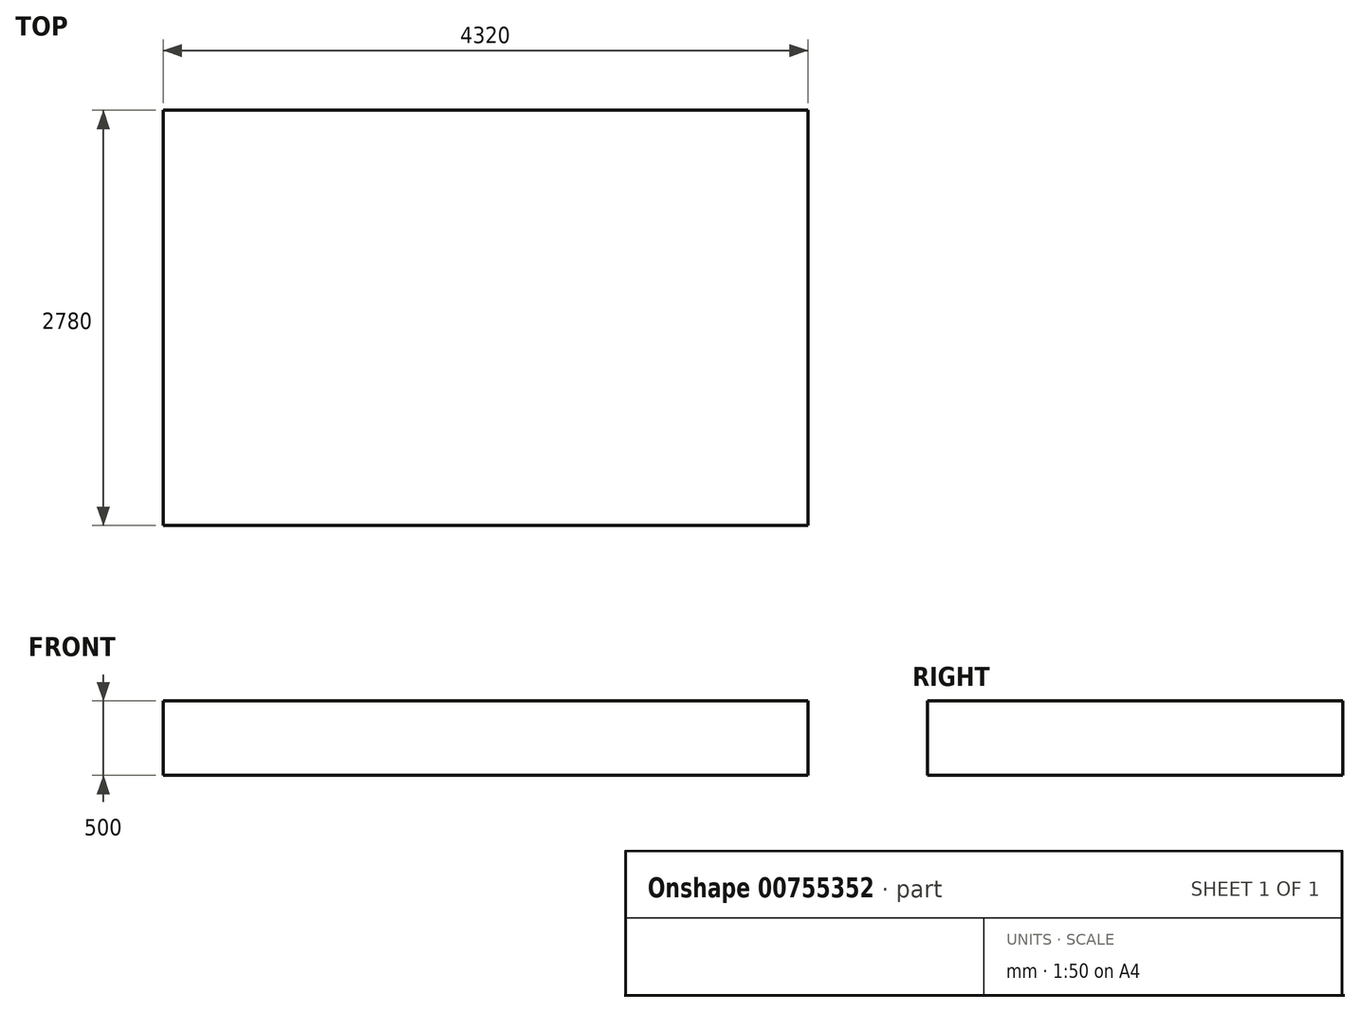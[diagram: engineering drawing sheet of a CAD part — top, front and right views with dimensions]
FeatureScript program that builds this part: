
annotation { "Feature Type Name" : "Feature", "Feature Type Description" : "" }
export const myFeature = defineFeature(function(context is Context, id is Id, definition is map)
    precondition{}
    {
        {
            var Q0;
            Q0=qCreatedBy(makeId("Top.planeOp"),FACE);
            var sketch = newSketch(context, id + "F0", { "sketchPlane" : qUnion([Q0])});
            skLineSegment(sketch, "E0.bottom", {"start": v(-2160, 1390) * mm, "end": v(2160, 1390) * mm});
            skLineSegment(sketch, "E0.top", {"start": v(-2160, -1390) * mm, "end": v(2160, -1390) * mm});
            skLineSegment(sketch, "E0.left", {"start": v(-2160, 1390) * mm, "end": v(-2160, -1390) * mm});
            skLineSegment(sketch, "E0.right", {"start": v(2160, 1390) * mm, "end": v(2160, -1390) * mm});
            skPoint(sketch, "E0.middle", {"position": v(0, 0) * mm});
            skSolve(sketch);
        }
        {
            var Q0;
            Q0 = qSketchRegion(id + "F0", true);
            extrude(context, id + "F1", {"entities" : qUnion([Q0]), "depth" : 500 * mm, "offsetDistance" : 25 * mm});
        }
    });
